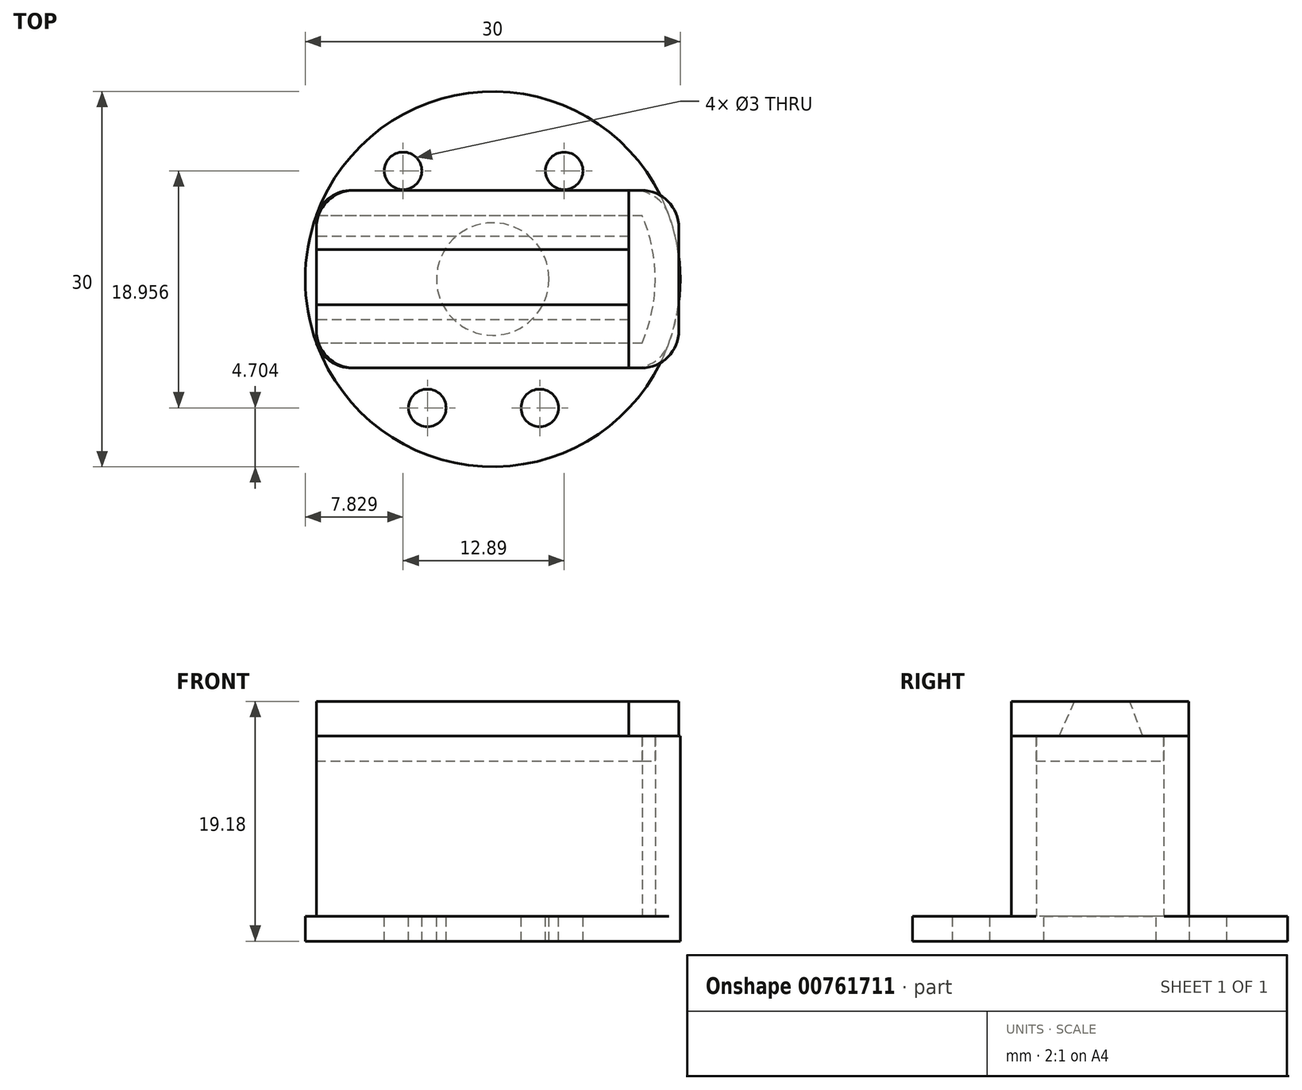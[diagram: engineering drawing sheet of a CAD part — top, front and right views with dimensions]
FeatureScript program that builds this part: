
annotation { "Feature Type Name" : "Feature", "Feature Type Description" : "" }
export const myFeature = defineFeature(function(context is Context, id is Id, definition is map)
    precondition{}
    {
        {
            var Q0;
            Q0=qCreatedBy(makeId("Top.planeOp"),FACE);
            var sketch = newSketch(context, id + "F0", { "sketchPlane" : qUnion([Q0])});
            skArc(sketch, "E0", {"start": v(-13.21, 7.1) * mm, "mid": v(-14.96, 1.1) * mm, "end": v(-14.1, -5.1) * mm});
            skCircle(sketch, "E1", {"center": v(0, 0) * mm, "radius": 5 * mm, "construction": true});
            skLineSegment(sketch, "E2", {"start": v(-14.1, 5.1) * mm, "end": v(14.1, 5.1) * mm});
            skLineSegment(sketch, "E3", {"start": v(-14.1, -5.1) * mm, "end": v(14.1, -5.1) * mm});
            skArc(sketch, "E4.trimOffspring", {"start": v(14.1, -5.1) * mm, "mid": v(15, 0) * mm, "end": v(14.1, 5.1) * mm});
            skLineSegment(sketch, "E5.0", {"start": v(-14.1, -7.1) * mm, "end": v(13.21, -7.1) * mm});
            skLineSegment(sketch, "E5.2", {"start": v(-13.21, 7.1) * mm, "end": v(13.21, 7.1) * mm});
            skArc(sketch, "E6", {"start": v(13.21, -7.1) * mm, "mid": v(15, 0) * mm, "end": v(13.21, 7.1) * mm});
            skArc(sketch, "E7", {"start": v(10.89, -7.1) * mm, "mid": v(13, 0) * mm, "end": v(10.89, 7.1) * mm});
            skArc(sketch, "E8.trimOffspring", {"start": v(-10.89, 7.1) * mm, "mid": v(-13, 0) * mm, "end": v(-10.89, -7.1) * mm});
            skArc(sketch, "E9.trimOffspring", {"start": v(-14.1, 5.1) * mm, "mid": v(-15, 0) * mm, "end": v(-14.1, -5.1) * mm});
            skLineSegment(sketch, "E10", {"start": v(0, -11.54) * mm, "end": v(0, 18.93) * mm, "construction": true});
            skPoint(sketch, "E10.endSnap0", {"position": v(0, 7.1) * mm});
            skLineSegment(sketch, "E11", {"start": v(-18.6, 0) * mm, "end": v(18.11, 0) * mm, "construction": true});
            skLineSegment(sketch, "E12", {"start": v(-14.1, -5.1) * mm, "end": v(-14.1, -7.1) * mm});
            skLineSegment(sketch, "E13", {"start": v(-13.21, 7.1) * mm, "end": v(-13.21, 7.1) * mm});
            skSolve(sketch);
        }
        {
            var Q0;
            {var subQ0=sQuery(id+"F0.wireOp",EDGE,"E12");Q0=makeQuery(id+"F0.imprint","IMPRINT",FACE,{"disambiguationData":[TD([[makeQuery(id+"F0.imprint","IMPRINT",EDGE,{"derivedFrom":subQ0}),1.0]])]});}
            var Q1;
            {var subQ0=sQuery(id+"F0.wireOp",EDGE,"E6");var subQ5=sQuery(id+"F0.wireOp",EDGE,"E5.0");var subQ6=makeQuery(id+"F0.imprint","INTERSECT",VERTEX,{"derivedFrom":[subQ5,subQ0]});Q1=makeQuery(id+"F0.imprint","IMPRINT",FACE,{"disambiguationData":[TD([[makeQuery(id+"F0.imprint","IMPRINT",EDGE,{"disambiguationData":[TD([[subQ6,1.0]])],"derivedFrom":subQ5}),1.0]])]});}
            var Q2;
            {var subQ0=sQuery(id+"F0.wireOp",EDGE,"E5.2");var subQ1=sQuery(id+"F0.wireOp",EDGE,"E0");var subQ2=makeQuery(id+"F0.imprint","INTERSECT",VERTEX,{"derivedFrom":[subQ1,subQ0]});Q2=makeQuery(id+"F0.imprint","IMPRINT",FACE,{"disambiguationData":[TD([[makeQuery(id+"F0.imprint","IMPRINT",EDGE,{"disambiguationData":[TD([[subQ2,-1.0]])],"derivedFrom":subQ1}),1.0]])]});}
            var Q3;
            {var subQ0=sQuery(id+"F0.wireOp",EDGE,"E6");var subQ5=sQuery(id+"F0.wireOp",EDGE,"E5.2");var subQ6=makeQuery(id+"F0.imprint","INTERSECT",VERTEX,{"derivedFrom":[subQ5,subQ0]});Q3=makeQuery(id+"F0.imprint","IMPRINT",FACE,{"disambiguationData":[TD([[makeQuery(id+"F0.imprint","IMPRINT",EDGE,{"disambiguationData":[TD([[subQ6,1.0]])],"derivedFrom":subQ5}),-1.0]])]});}
            var Q4;
            {var subQ0=sQuery(id+"F0.wireOp",EDGE,"E8.trimOffspring");var subQ1=sQuery(id+"F0.wireOp",EDGE,"E3");var subQ2=makeQuery(id+"F0.imprint","INTERSECT",VERTEX,{"derivedFrom":[subQ1,subQ0]});Q4=makeQuery(id+"F0.imprint","IMPRINT",FACE,{"disambiguationData":[TD([[makeQuery(id+"F0.imprint","IMPRINT",EDGE,{"disambiguationData":[TD([[subQ2,-1.0]])],"derivedFrom":subQ1}),-1.0]])]});}
            var Q5;
            {var subQ1=sQuery(id+"F0.wireOp",EDGE,"E4.trimOffspring");Q5=makeQuery(id+"F0.imprint","IMPRINT",FACE,{"disambiguationData":[TD([[makeQuery(id+"F0.imprint","IMPRINT",EDGE,{"derivedFrom":subQ1}),1.0]])]});}
            var Q6;
            {var subQ0=sQuery(id+"F0.wireOp",EDGE,"E8.trimOffspring");var subQ1=sQuery(id+"F0.wireOp",EDGE,"E2");var subQ2=makeQuery(id+"F0.imprint","INTERSECT",VERTEX,{"derivedFrom":[subQ1,subQ0]});Q6=makeQuery(id+"F0.imprint","IMPRINT",FACE,{"disambiguationData":[TD([[makeQuery(id+"F0.imprint","IMPRINT",EDGE,{"disambiguationData":[TD([[subQ2,-1.0]])],"derivedFrom":subQ1}),1.0]])]});}
            extrude(context, id + "F1", {"entities" : qUnion([Q0, Q1, Q2, Q3, Q4, Q5, Q6]), "depth" : 14.4 * mm, "offsetDistance" : 25 * mm});
        }
        {
            var Q0;
            Q0=makeQuery(id+"F1.opExtrude","CAP_FACE",FACE,{"disambiguationData":[OSD([sQuery(id+"F0.wireOp",EDGE,"E0"),sQuery(id+"F0.wireOp",EDGE,"E2"),sQuery(id+"F0.wireOp",EDGE,"E3"),sQuery(id+"F0.wireOp",EDGE,"E4.trimOffspring"),sQuery(id+"F0.wireOp",EDGE,"E5.0"),sQuery(id+"F0.wireOp",EDGE,"E5.2"),sQuery(id+"F0.wireOp",EDGE,"E6"),sQuery(id+"F0.wireOp",EDGE,"E7"),sQuery(id+"F0.wireOp",EDGE,"E12")])],"isStart":false});
            var sketch = newSketch(context, id + "F2", { "sketchPlane" : qUnion([Q0])});
            skLineSegment(sketch, "E14", {"start": v(-14.1, -5.1) * mm, "end": v(-14.1, 5.1) * mm});
            skSolve(sketch);
        }
        {
            var Q0;
            Q0 = qSketchRegion(id + "F2", true);
            var Q1;
            Q1=makeQuery(id+"F2.imprint","IMPRINT",FACE,{"disambiguationData":[TD([[makeQuery(id+"F2.imprint","IMPRINT",EDGE,{"derivedFrom":sQuery(id+"F2.wireOp",EDGE,"E14")}),-1.0]])]});
            extrude(context, id + "F3", {"entities" : qUnion([Q0, Q1]), "oppositeDirection" : true, "depth" : 2 * mm, "offsetDistance" : 25 * mm});
        }
        {
            var Q0;
            Q0=makeQuery(id+"F3.opExtrude","SWEPT_FACE",FACE,{"disambiguationData":[OSD([sQuery(id+"F2.wireOp",EDGE,"E14")])]});
            var sketch = newSketch(context, id + "F4", { "sketchPlane" : qUnion([Q0])});
            skLineSegment(sketch, "E15.bottom", {"start": v(5.43, 14.4) * mm, "end": v(-4.77, 14.4) * mm});
            skLineSegment(sketch, "E15.top", {"start": v(7.1, 17.18) * mm, "end": v(2.04, 17.18) * mm});
            skLineSegment(sketch, "E15.left", {"start": v(7.1, 14.4) * mm, "end": v(7.1, 17.18) * mm});
            skLineSegment(sketch, "E15.right", {"start": v(-7.1, 14.4) * mm, "end": v(-7.1, 17.18) * mm});
            skPoint(sketch, "E16.endSnap0", {"position": v(0, 17.18) * mm});
            skLineSegment(sketch, "E17", {"start": v(-3.42, 14.4) * mm, "end": v(-2.38, 17.18) * mm});
            skLineSegment(sketch, "E18.MirrorCS", {"start": v(3.26, 14.4) * mm, "end": v(2.04, 17.18) * mm});
            skLineSegment(sketch, "E19.trimOffspring", {"start": v(-2.38, 17.18) * mm, "end": v(-7.1, 17.18) * mm});
            skPoint(sketch, "E20.orphan", {"position": v(0, 22.54) * mm});
            skPoint(sketch, "E16.start.orphan", {"position": v(0, 9.9) * mm});
            skLineSegment(sketch, "E21", {"start": v(-2.38, 17.18) * mm, "end": v(2.04, 17.18) * mm});
            skLineSegment(sketch, "E22", {"start": v(-7.1, 14.4) * mm, "end": v(7.1, 14.4) * mm});
            skSolve(sketch);
        }
        {
            var Q0;
            Q0=makeQuery(id+"F4.imprint","IMPRINT",FACE,{"disambiguationData":[TD([[makeQuery(id+"F4.imprint","IMPRINT",EDGE,{"derivedFrom":sQuery(id+"F4.wireOp",EDGE,"E15.top")}),1.0]])]});
            var Q1;
            {var subQ0=sQuery(id+"F4.wireOp",EDGE,"E15.right");Q1=makeQuery(id+"F4.imprint","IMPRINT",FACE,{"disambiguationData":[TD([[makeQuery(id+"F4.imprint","IMPRINT",EDGE,{"derivedFrom":subQ0}),-1.0]])]});}
            var Q2;
            {var subQ0=sQuery(id+"F4.wireOp",EDGE,"E17");Q2=makeQuery(id+"F4.imprint","IMPRINT",FACE,{"disambiguationData":[TD([[makeQuery(id+"F4.imprint","IMPRINT",EDGE,{"derivedFrom":subQ0}),-1.0]])]});}
            extrude(context, id + "F5", {"entities" : qUnion([Q0, Q1, Q2]), "oppositeDirection" : true, "depth" : 29 * mm, "offsetDistance" : 25 * mm});
        }
        {
            var Q0;
            Q0 = qSketchRegion(id + "F4", true);
            extrude(context, id + "F6", {"entities" : qUnion([Q0]), "oppositeDirection" : true, "depth" : 25 * mm, "offsetDistance" : 25 * mm});
        }
        {
            var Q0;
            {var subQ0=sQuery(id+"F4.wireOp",EDGE,"E17");Q0=makeQuery(id+"F4.imprint","IMPRINT",FACE,{"disambiguationData":[TD([[makeQuery(id+"F4.imprint","IMPRINT",EDGE,{"derivedFrom":subQ0}),-1.0]])]});}
            extrude(context, id + "F7", {"entities" : qUnion([Q0]), "operationType" : NewBodyOperationType.REMOVE, "oppositeDirection" : true, "depth" : 25 * mm, "offsetDistance" : 25 * mm});
        }
        {
            var Q0;
            Q0=makeQuery(id+"F5.opExtrude","CAP_EDGE",EDGE,{"disambiguationData":[OSD([sQuery(id+"F4.wireOp",EDGE,"E15.right")])],"isStart":false});
            var Q1;
            Q1=makeQuery(id+"F5.opExtrude","CAP_EDGE",EDGE,{"disambiguationData":[OSD([sQuery(id+"F4.wireOp",EDGE,"E15.left")])],"isStart":false});
            var Q2;
            Q2=makeQuery(id+"F1.opExtrude","SWEPT_EDGE",EDGE,{"disambiguationData":[OSD([sQuery(id+"F0.wireOp",EDGE,"E5.2"),sQuery(id+"F0.wireOp",EDGE,"E6")])]});
            var Q3;
            Q3=makeQuery(id+"F1.opExtrude","SWEPT_EDGE",EDGE,{"disambiguationData":[OSD([sQuery(id+"F0.wireOp",EDGE,"E5.0"),sQuery(id+"F0.wireOp",EDGE,"E6")])]});
            var Q4;
            Q4=makeQuery(id+"F5.opExtrude","CAP_EDGE",EDGE,{"disambiguationData":[OSD([sQuery(id+"F4.wireOp",EDGE,"E15.left")])],"isStart":true});
            var Q5;
            Q5=makeQuery(id+"F1.opExtrude","SWEPT_EDGE",EDGE,{"disambiguationData":[OSD([sQuery(id+"F0.wireOp",EDGE,"E5.0"),sQuery(id+"F0.wireOp",EDGE,"E12")])]});
            var Q6;
            Q6=makeQuery(id+"F5.opExtrude","CAP_EDGE",EDGE,{"disambiguationData":[OSD([sQuery(id+"F4.wireOp",EDGE,"E15.right")])],"isStart":true});
            var Q7;
            {var subQ0=sQuery(id+"F0.wireOp",EDGE,"E5.2");Q7=qUnion([makeQuery(id+"F1.opExtrude","SWEPT_EDGE",EDGE,{"disambiguationData":[OSD([sQuery(id+"F0.wireOp",EDGE,"E0"),subQ0])]}),makeQuery(id+"F1.opExtrude","SWEPT_EDGE",EDGE,{"disambiguationData":[OSD([subQ0,sQuery(id+"F0.wireOp",EDGE,"E6")])]})]);}
            fillet(context, id + "F8", {"entities" : qUnion([Q0, Q1, Q2, Q3, Q4, Q5, Q6, Q7]), "radius" : 3 * mm, "tangentPropagation" : true, "allowEdgeOverflow" : false});
        }
        {
            var Q0;
            Q0=makeQuery(id+"F6.opExtrude","CAP_EDGE",EDGE,{"disambiguationData":[OSD([sQuery(id+"F4.wireOp",EDGE,"E15.right")])],"isStart":true});
            var Q1;
            Q1=makeQuery(id+"F6.opExtrude","CAP_EDGE",EDGE,{"disambiguationData":[OSD([sQuery(id+"F4.wireOp",EDGE,"E15.left")])],"isStart":true});
            fillet(context, id + "F9", {"entities" : qUnion([Q0, Q1]), "radius" : 3 * mm, "tangentPropagation" : true, "allowEdgeOverflow" : false});
        }
        {
            var Q0;
            Q0=qCreatedBy(makeId("Top.planeOp"),FACE);
            var sketch = newSketch(context, id + "F10", { "sketchPlane" : qUnion([Q0])});
            skCircle(sketch, "E23", {"center": v(0, 0) * mm, "radius": 15 * mm});
            skPoint(sketch, "E24.center", {"position": v(-0.73, -0.26) * mm});
            skCircle(sketch, "E25", {"center": v(3.77, -10.3) * mm, "radius": 1.5 * mm});
            skCircle(sketch, "E26", {"center": v(-5.23, -10.3) * mm, "radius": 1.5 * mm});
            skCircle(sketch, "E27.1.0", {"center": v(5.72, 8.65) * mm, "radius": 1.5 * mm});
            skCircle(sketch, "E27.2.1", {"center": v(-7.17, 8.66) * mm, "radius": 1.5 * mm});
            skCircle(sketch, "E28", {"center": v(0, 0) * mm, "radius": 4.5 * mm});
            skArc(sketch, "E29", {"start": v(0, 5) * mm, "mid": v(0, 5) * mm, "end": v(0, 5) * mm, "construction": true});
            skLineSegment(sketch, "E30", {"start": v(-14.15, -5) * mm, "end": v(14.15, -5) * mm});
            skLineSegment(sketch, "E31", {"start": v(-14.14, 5) * mm, "end": v(14.14, 5) * mm});
            skPoint(sketch, "E27.1.1.center.orphan", {"position": v(10.22, 0.86) * mm});
            skPoint(sketch, "E24.1.0.center.orphan", {"position": v(-11.12, -6.26) * mm});
            skPoint(sketch, "E32.trimOffspring.end.orphan", {"position": v(9.66, -6.26) * mm});
            skPoint(sketch, "E33.orphan", {"position": v(-0.73, 11.73) * mm});
            skSolve(sketch);
        }
        {
            var Q0;
            Q0 = qSketchRegion(id + "F10", true);
            extrude(context, id + "F11", {"entities" : qUnion([Q0]), "operationType" : NewBodyOperationType.ADD, "oppositeDirection" : true, "depth" : 2 * mm, "offsetDistance" : 25 * mm});
        }
    });
